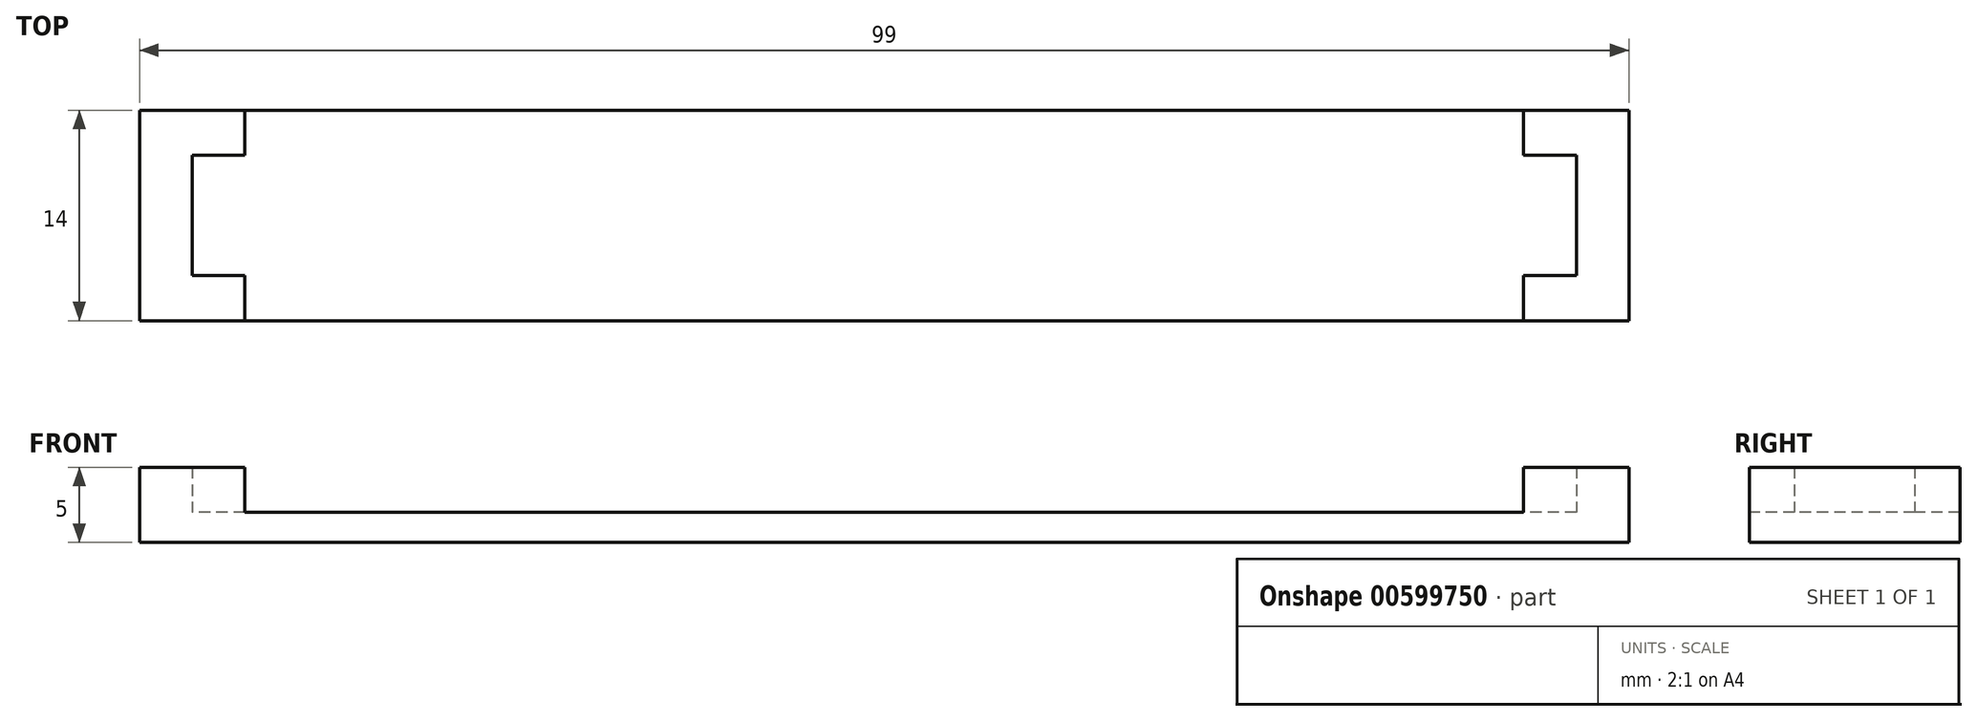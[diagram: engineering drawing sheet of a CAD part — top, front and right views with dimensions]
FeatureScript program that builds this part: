
annotation { "Feature Type Name" : "Feature", "Feature Type Description" : "" }
export const myFeature = defineFeature(function(context is Context, id is Id, definition is map)
    precondition{}
    {
        {
            var Q0;
            Q0=qCreatedBy(makeId("Top.planeOp"),FACE);
            var sketch = newSketch(context, id + "F0", { "sketchPlane" : qUnion([Q0])});
            skLineSegment(sketch, "E0.bottom", {"start": v(49.5, 7) * mm, "end": v(-49.5, 7) * mm});
            skLineSegment(sketch, "E0.top", {"start": v(49.5, -7) * mm, "end": v(-49.5, -7) * mm});
            skLineSegment(sketch, "E0.left", {"start": v(49.5, 7) * mm, "end": v(49.5, -7) * mm});
            skLineSegment(sketch, "E0.right", {"start": v(-49.5, 7) * mm, "end": v(-49.5, -7) * mm});
            skPoint(sketch, "E0.middle", {"position": v(0, 0) * mm});
            skLineSegment(sketch, "E1", {"start": v(42.5, 7) * mm, "end": v(42.5, 4) * mm});
            skLineSegment(sketch, "E2", {"start": v(42.5, 4) * mm, "end": v(46, 4) * mm});
            skLineSegment(sketch, "E3", {"start": v(46, 4) * mm, "end": v(46, -4) * mm});
            skLineSegment(sketch, "E4", {"start": v(46, -4) * mm, "end": v(42.5, -4) * mm});
            skLineSegment(sketch, "E5", {"start": v(42.5, -4) * mm, "end": v(42.5, -7) * mm});
            skLineSegment(sketch, "E6", {"start": v(-42.5, 7) * mm, "end": v(-42.5, 4) * mm});
            skLineSegment(sketch, "E7", {"start": v(-42.5, 4) * mm, "end": v(-46, 4) * mm});
            skLineSegment(sketch, "E8", {"start": v(-46, 4) * mm, "end": v(-46, -4) * mm});
            skLineSegment(sketch, "E9", {"start": v(-46, -4) * mm, "end": v(-42.5, -4) * mm});
            skLineSegment(sketch, "E10", {"start": v(-42.5, -4) * mm, "end": v(-42.5, -7) * mm});
            skSolve(sketch);
        }
        {
            var Q0;
            {var subQ2=sQuery(id+"F0.wireOp",EDGE,"E1");Q0=makeQuery(id+"F0.imprint","IMPRINT",FACE,{"disambiguationData":[TD([[makeQuery(id+"F0.imprint","IMPRINT",EDGE,{"derivedFrom":subQ2}),-1.0]])]});}
            extrude(context, id + "F1", {"entities" : qUnion([Q0]), "depth" : 2 * mm, "offsetDistance" : 25 * mm});
        }
        {
            var Q0;
            {var subQ1=sQuery(id+"F0.wireOp",EDGE,"E0.right");Q0=makeQuery(id+"F0.imprint","IMPRINT",FACE,{"disambiguationData":[TD([[makeQuery(id+"F0.imprint","IMPRINT",EDGE,{"derivedFrom":subQ1}),1.0]])]});}
            extrude(context, id + "F2", {"entities" : qUnion([Q0]), "operationType" : NewBodyOperationType.ADD, "depth" : 5 * mm, "offsetDistance" : 25 * mm});
        }
        {
            var Q0;
            {var subQ0=sQuery(id+"F0.wireOp",EDGE,"E0.left");Q0=makeQuery(id+"F0.imprint","IMPRINT",FACE,{"disambiguationData":[TD([[makeQuery(id+"F0.imprint","IMPRINT",EDGE,{"derivedFrom":subQ0}),-1.0]])]});}
            extrude(context, id + "F3", {"entities" : qUnion([Q0]), "operationType" : NewBodyOperationType.ADD, "depth" : 5 * mm, "offsetDistance" : 25 * mm});
        }
    });
